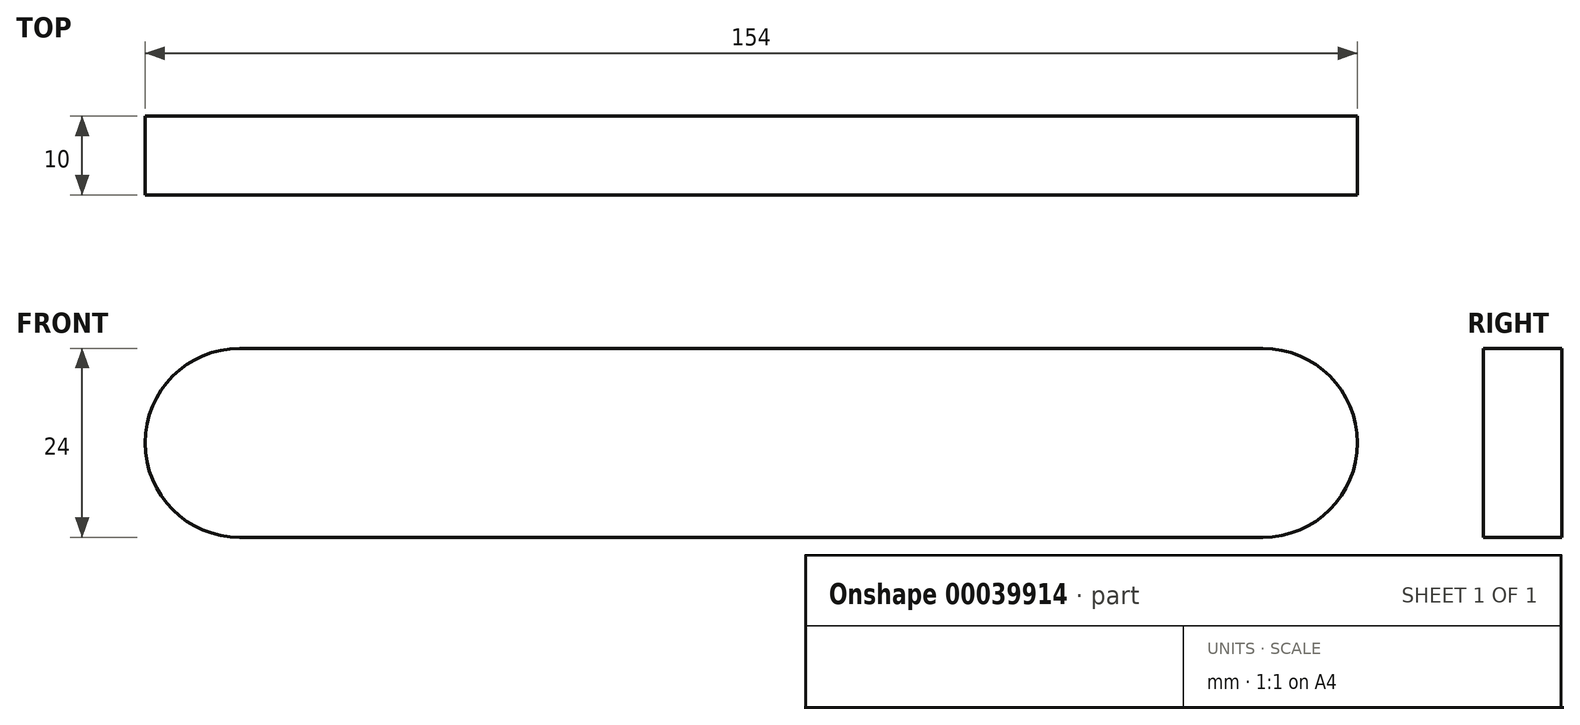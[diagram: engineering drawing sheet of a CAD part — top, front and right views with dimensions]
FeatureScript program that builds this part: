
annotation { "Feature Type Name" : "Feature", "Feature Type Description" : "" }
export const myFeature = defineFeature(function(context is Context, id is Id, definition is map)
    precondition{}
    {
        {
            var Q0;
            Q0=qCreatedBy(makeId("Front.planeOp"),FACE);
            var sketch = newSketch(context, id + "F0", { "sketchPlane" : qUnion([Q0])});
            skLineSegment(sketch, "E0.rect.bottom", {"start": v(65, -12) * mm, "end": v(-65, -12) * mm});
            skLineSegment(sketch, "E0.rect.top", {"start": v(65, 12) * mm, "end": v(-65, 12) * mm});
            skLineSegment(sketch, "E0.rect.left", {"start": v(65, -12) * mm, "end": v(65, 12) * mm});
            skLineSegment(sketch, "E0.rect.right", {"start": v(-65, -12) * mm, "end": v(-65, 12) * mm});
            skPoint(sketch, "E0.rect.middle", {"position": v(0, 0) * mm});
            skArc(sketch, "E1", {"start": v(-65, 12) * mm, "mid": v(-77, 0) * mm, "end": v(-65, -12) * mm});
            skArc(sketch, "E2", {"start": v(65, -12) * mm, "mid": v(77, 0) * mm, "end": v(65, 12) * mm});
            skSolve(sketch);
        }
        {
            var Q0;
            Q0 = qSketchRegion(id + "F0", true);
            extrude(context, id + "F1", {"entities" : qUnion([Q0]), "depth" : 10 * mm});
        }
    });
